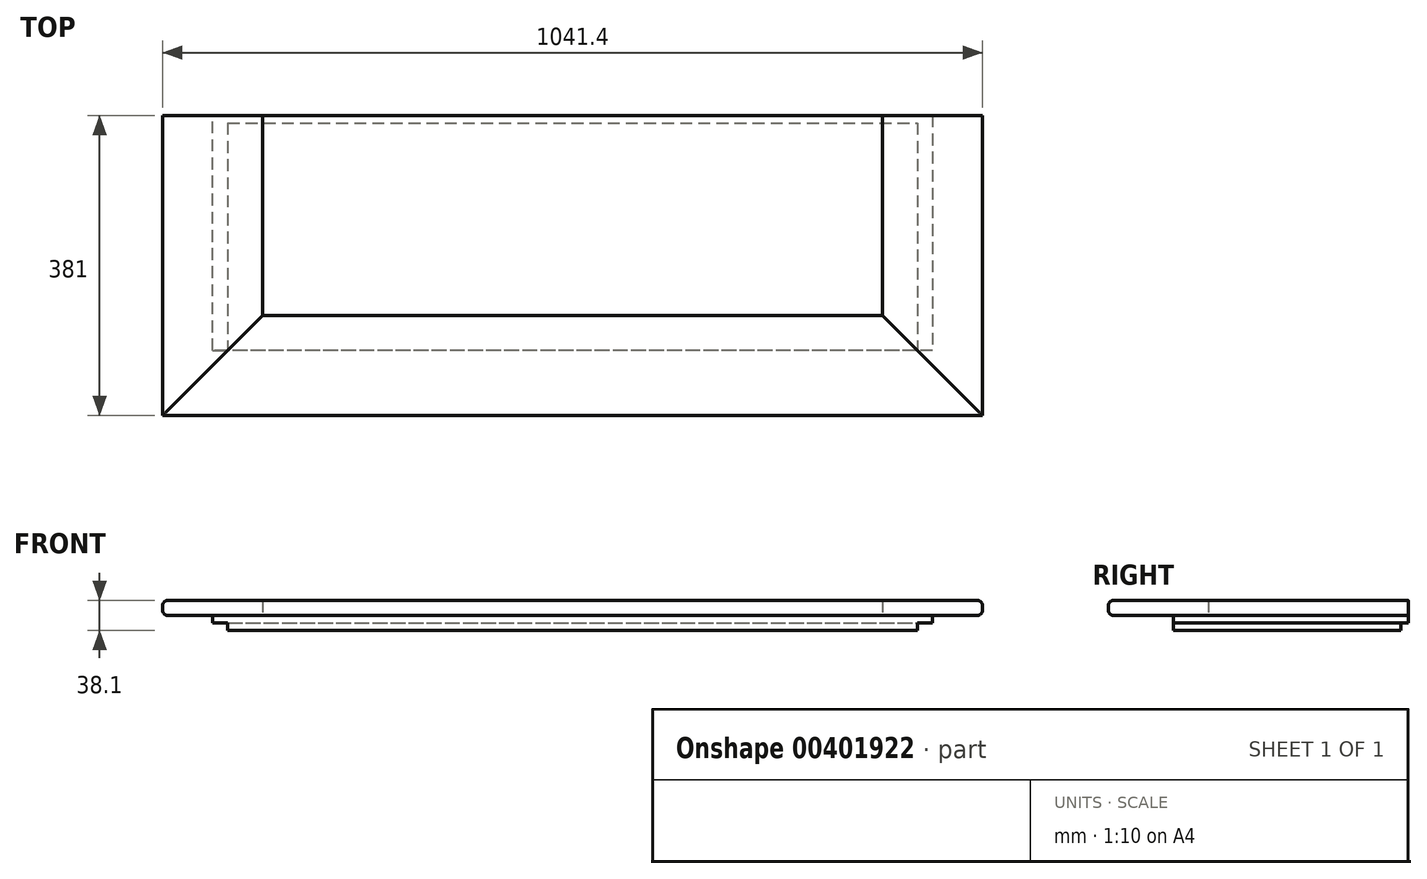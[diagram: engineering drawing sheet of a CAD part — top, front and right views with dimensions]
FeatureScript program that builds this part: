
annotation { "Feature Type Name" : "Feature", "Feature Type Description" : "" }
export const myFeature = defineFeature(function(context is Context, id is Id, definition is map)
    precondition{}
    {
        {
            var Q0;
            Q0=qCreatedBy(makeId("Top.planeOp"),FACE);
            var sketch = newSketch(context, id + "F0", { "sketchPlane" : qUnion([Q0])});
            skLineSegment(sketch, "E0.bottom", {"start": v(457.2, -149.22) * mm, "end": v(-457.2, -149.23) * mm});
            skLineSegment(sketch, "E0.top", {"start": v(457.2, 149.23) * mm, "end": v(-457.2, 149.22) * mm});
            skLineSegment(sketch, "E0.left", {"start": v(457.2, -149.22) * mm, "end": v(457.2, 149.23) * mm});
            skLineSegment(sketch, "E0.right", {"start": v(-457.2, -149.23) * mm, "end": v(-457.2, 149.22) * mm});
            skPoint(sketch, "E0.middle", {"position": v(0, 0) * mm});
            skSolve(sketch);
        }
        {
            var Q0;
            Q0=qSketchRegion(id+"F0",true);
            extrude(context, id + "F1", {"entities" : qUnion([Q0]), "depth" : 19.05 * mm});
        }
        {
            var Q0;
            Q0=makeQuery(id+"F1.opExtrude","SWEPT_FACE",FACE,{"disambiguationData":[OSD([sQuery(id+"F0.wireOp",EDGE,"E0.left")])]});
            var sketch = newSketch(context, id + "F2", { "sketchPlane" : qUnion([Q0])});
            skLineSegment(sketch, "E1.bottom", {"start": v(149.23, 9.53) * mm, "end": v(139.7, 9.53) * mm});
            skLineSegment(sketch, "E1.top", {"start": v(149.23, 0) * mm, "end": v(139.7, 0) * mm});
            skLineSegment(sketch, "E1.left", {"start": v(149.23, 9.53) * mm, "end": v(149.23, 0) * mm});
            skLineSegment(sketch, "E1.right", {"start": v(139.7, 9.53) * mm, "end": v(139.7, 0) * mm});
            skSolve(sketch);
        }
        {
            var Q0;
            Q0=qSketchRegion(id+"F2",true);
            extrude(context, id + "F3", {"entities" : qUnion([Q0]), "operationType" : NewBodyOperationType.REMOVE, "endBound" : BoundingType.THROUGH_ALL, "oppositeDirection" : true, "depth" : 25.4 * mm});
        }
        {
            var Q0;
            Q0=makeQuery(id+"F1.opExtrude","SWEPT_FACE",FACE,{"disambiguationData":[OSD([sQuery(id+"F0.wireOp",EDGE,"E0.bottom")])]});
            var sketch = newSketch(context, id + "F4", { "sketchPlane" : qUnion([Q0])});
            skLineSegment(sketch, "E2.bottom", {"start": v(-457.2, 9.53) * mm, "end": v(-438.15, 9.53) * mm});
            skLineSegment(sketch, "E2.top", {"start": v(-457.2, 0) * mm, "end": v(-438.15, 0) * mm});
            skLineSegment(sketch, "E2.left", {"start": v(-457.2, 9.53) * mm, "end": v(-457.2, 0) * mm});
            skLineSegment(sketch, "E2.right", {"start": v(-438.15, 9.53) * mm, "end": v(-438.15, 0) * mm});
            skLineSegment(sketch, "E3", {"start": v(0, 19.05) * mm, "end": v(0, 0) * mm, "construction": true});
            skLineSegment(sketch, "E4.MirrorCS", {"start": v(438.15, 9.52) * mm, "end": v(438.15, 0) * mm});
            skLineSegment(sketch, "E5.MirrorCS", {"start": v(457.2, 9.52) * mm, "end": v(457.2, 0) * mm});
            skLineSegment(sketch, "E6.MirrorCS", {"start": v(457.2, 0) * mm, "end": v(438.15, 0) * mm});
            skLineSegment(sketch, "E7.MirrorCS", {"start": v(457.2, 9.53) * mm, "end": v(438.15, 9.53) * mm});
            skSolve(sketch);
        }
        {
            var Q0;
            Q0=qSketchRegion(id+"F4",true);
            extrude(context, id + "F5", {"entities" : qUnion([Q0]), "operationType" : NewBodyOperationType.REMOVE, "endBound" : BoundingType.THROUGH_ALL, "oppositeDirection" : true, "depth" : 25.4 * mm});
        }
        {
            var Q0;
            Q0=makeQuery(id+"F1.opExtrude","CAP_FACE",FACE,{"disambiguationData":[OSD([sQuery(id+"F0.wireOp",EDGE,"E0.bottom"),sQuery(id+"F0.wireOp",EDGE,"E0.top"),sQuery(id+"F0.wireOp",EDGE,"E0.left"),sQuery(id+"F0.wireOp",EDGE,"E0.right")])],"isStart":false});
            var sketch = newSketch(context, id + "F6", { "sketchPlane" : qUnion([Q0])});
            skLineSegment(sketch, "E8.bottom", {"start": v(-393.7, -104.78) * mm, "end": v(393.7, -104.77) * mm});
            skLineSegment(sketch, "E8.top", {"start": v(-520.7, -231.78) * mm, "end": v(520.7, -231.77) * mm});
            skLineSegment(sketch, "E9", {"start": v(-520.7, -231.78) * mm, "end": v(-393.7, -104.78) * mm});
            skLineSegment(sketch, "E10", {"start": v(520.7, -231.77) * mm, "end": v(393.7, -104.77) * mm});
            skSolve(sketch);
        }
        {
            var Q0;
            Q0=qSketchRegion(id+"F6",true);
            extrude(context, id + "F7", {"entities" : qUnion([Q0]), "depth" : 19.05 * mm});
        }
        {
            var Q0;
            Q0=makeQuery(id+"F1.opExtrude","CAP_FACE",FACE,{"disambiguationData":[OSD([sQuery(id+"F0.wireOp",EDGE,"E0.bottom"),sQuery(id+"F0.wireOp",EDGE,"E0.top"),sQuery(id+"F0.wireOp",EDGE,"E0.left"),sQuery(id+"F0.wireOp",EDGE,"E0.right")])],"isStart":false});
            var sketch = newSketch(context, id + "F8", { "sketchPlane" : qUnion([Q0])});
            skLineSegment(sketch, "E11.bottom", {"start": v(-520.7, 149.22) * mm, "end": v(-393.7, 149.22) * mm});
            skLineSegment(sketch, "E11.left", {"start": v(-520.7, 149.22) * mm, "end": v(-520.7, -231.78) * mm});
            skLineSegment(sketch, "E11.right", {"start": v(-393.7, 149.22) * mm, "end": v(-393.7, -104.77) * mm});
            skLineSegment(sketch, "E12", {"start": v(-520.7, -231.78) * mm, "end": v(-393.7, -104.77) * mm});
            skSolve(sketch);
        }
        {
            var Q0;
            Q0=qSketchRegion(id+"F8",true);
            extrude(context, id + "F9", {"entities" : qUnion([Q0]), "depth" : 19.05 * mm});
        }
        {
            var Q0;
            Q0=makeQuery(id+"F1.opExtrude","CAP_FACE",FACE,{"disambiguationData":[OSD([sQuery(id+"F0.wireOp",EDGE,"E0.bottom"),sQuery(id+"F0.wireOp",EDGE,"E0.top"),sQuery(id+"F0.wireOp",EDGE,"E0.left"),sQuery(id+"F0.wireOp",EDGE,"E0.right")])],"isStart":false});
            var sketch = newSketch(context, id + "F10", { "sketchPlane" : qUnion([Q0])});
            skLineSegment(sketch, "E13.bottom", {"start": v(393.7, 149.23) * mm, "end": v(520.7, 149.23) * mm});
            skLineSegment(sketch, "E13.left", {"start": v(393.7, 149.23) * mm, "end": v(393.7, -104.78) * mm});
            skLineSegment(sketch, "E13.right", {"start": v(520.7, 149.23) * mm, "end": v(520.7, -231.77) * mm});
            skLineSegment(sketch, "E14", {"start": v(520.7, -231.77) * mm, "end": v(393.7, -104.77) * mm});
            skSolve(sketch);
        }
        {
            var Q0;
            Q0=qSketchRegion(id+"F10",true);
            extrude(context, id + "F11", {"entities" : qUnion([Q0]), "depth" : 19.05 * mm});
        }
        {
            var Q0;
            Q0=makeQuery(id+"F7.opExtrude","CAP_EDGE",EDGE,{"disambiguationData":[OSD([sQuery(id+"F6.wireOp",EDGE,"E8.top")])],"isStart":false});
            var Q1;
            Q1=makeQuery(id+"F7.opExtrude","CAP_EDGE",EDGE,{"disambiguationData":[OSD([sQuery(id+"F6.wireOp",EDGE,"E8.top")])],"isStart":true});
            var Q2;
            Q2=makeQuery(id+"F11.opExtrude","CAP_EDGE",EDGE,{"disambiguationData":[OSD([sQuery(id+"F10.wireOp",EDGE,"E13.right")])],"isStart":true});
            var Q3;
            Q3=makeQuery(id+"F11.opExtrude","CAP_EDGE",EDGE,{"disambiguationData":[OSD([sQuery(id+"F10.wireOp",EDGE,"E13.right")])],"isStart":false});
            var Q4;
            Q4=makeQuery(id+"F9.opExtrude","CAP_EDGE",EDGE,{"disambiguationData":[OSD([sQuery(id+"F8.wireOp",EDGE,"E11.left")])],"isStart":false});
            var Q5;
            Q5=makeQuery(id+"F9.opExtrude","CAP_EDGE",EDGE,{"disambiguationData":[OSD([sQuery(id+"F8.wireOp",EDGE,"E11.left")])],"isStart":true});
            fillet(context, id + "F12", {"entities" : qUnion([Q0, Q1, Q2, Q3, Q4, Q5]), "radius" : 6.35 * mm, "tangentPropagation" : true, "allowEdgeOverflow" : false});
        }
    });
